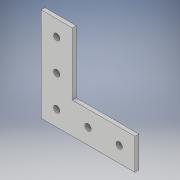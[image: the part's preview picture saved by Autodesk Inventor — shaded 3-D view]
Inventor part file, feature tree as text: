
AUTODESK INVENTOR PART (.ipt)
format: ipt  version: 2018 (Build 220112000, 112)  size: 111,104 bytes
history: native  units: in
note: dims shown in document units (in); Inventor stores cm internally (conversion verified against a paired STEP export)
features: extrude x1, sketch x1
ambient origin geometry x8: Origin, YZ Plane, XZ Plane, XY Plane, X Axis, Y Axis, Z Axis, Center Point
bodies: Solid1 (feature_tree)
feature tree (2):
  extrude  "Extrusion1"  Depth=3.0in
  sketch  "Sketch1"  dims[d0=1.0in d1=3.0in d2=3.0in d3=1.0in d4=0.5in d5=1.0in d6=1.0in d7=1.0in d8=1.0in d9=0.2031in d10=0.125in d11=0.0in]
